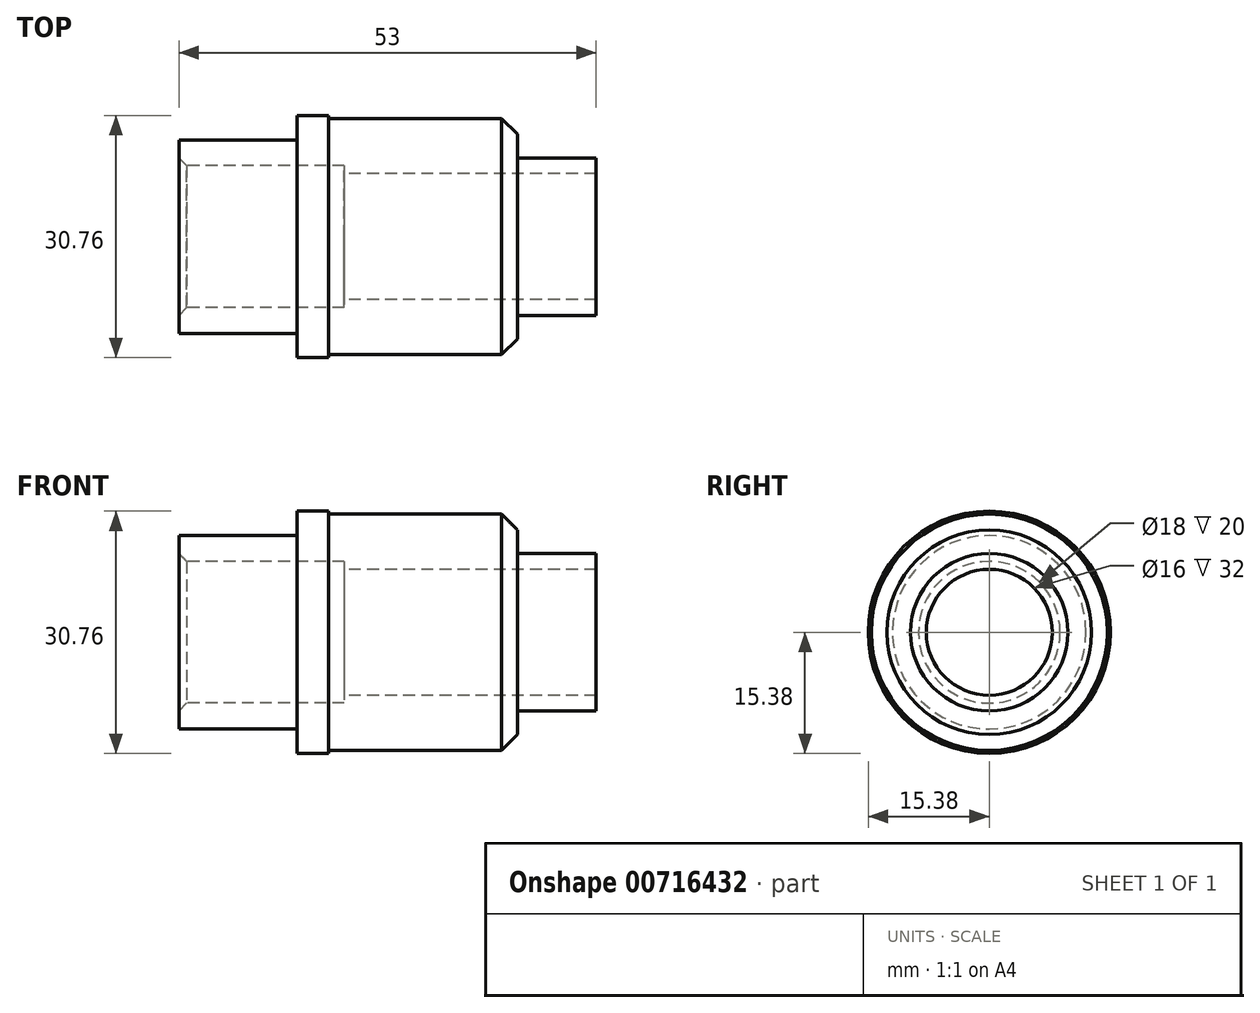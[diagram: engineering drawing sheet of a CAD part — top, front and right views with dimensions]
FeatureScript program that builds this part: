
annotation { "Feature Type Name" : "Feature", "Feature Type Description" : "" }
export const myFeature = defineFeature(function(context is Context, id is Id, definition is map)
    precondition{}
    {
        {
            var Q0;
            Q0=qCreatedBy(makeId("Top.planeOp"),FACE);
            var sketch = newSketch(context, id + "F0", { "sketchPlane" : qUnion([Q0])});
            skLineSegment(sketch, "E0", {"start": v(-54.51, 0) * mm, "end": v(76.36, 0) * mm, "construction": true});
            skLineSegment(sketch, "E1", {"start": v(21, 9) * mm, "end": v(1, 9) * mm});
            skLineSegment(sketch, "E2", {"start": v(0, 10) * mm, "end": v(0, 12.3) * mm});
            skLineSegment(sketch, "E3", {"start": v(0, 12.3) * mm, "end": v(15, 12.3) * mm});
            skLineSegment(sketch, "E4", {"start": v(15, 12.3) * mm, "end": v(15, 15.38) * mm});
            skLineSegment(sketch, "E5", {"start": v(15, 15.38) * mm, "end": v(19, 15.38) * mm});
            skLineSegment(sketch, "E6", {"start": v(19, 15) * mm, "end": v(19, 15.38) * mm});
            skLineSegment(sketch, "E7", {"start": v(19, 15) * mm, "end": v(41, 15) * mm});
            skLineSegment(sketch, "E8", {"start": v(43, 13) * mm, "end": v(43, 10) * mm});
            skLineSegment(sketch, "E9", {"start": v(43, 10) * mm, "end": v(53, 10) * mm});
            skLineSegment(sketch, "E10", {"start": v(53, 10) * mm, "end": v(53, 8) * mm});
            skLineSegment(sketch, "E11", {"start": v(53, 8) * mm, "end": v(21, 8) * mm});
            skLineSegment(sketch, "E12", {"start": v(21, 8) * mm, "end": v(21, 9) * mm});
            skLineSegment(sketch, "E13", {"start": v(41, 15) * mm, "end": v(43, 13) * mm});
            skLineSegment(sketch, "E14", {"start": v(0, 10) * mm, "end": v(1, 9) * mm});
            skSolve(sketch);
        }
        {
            var Q0;
            Q0=qSketchRegion(id+"F0",true);
            var Q1;
            Q1=sQuery(id+"F0.wireOp",EDGE,"E0");
            revolve(context, id + "F1", {"surfaceOperationType" : NewSurfaceOperationType.NEW, "entities" : qUnion([Q0]), "axis" : qUnion([Q1]), "revolveType" : RevolveType.FULL});
        }
    });
